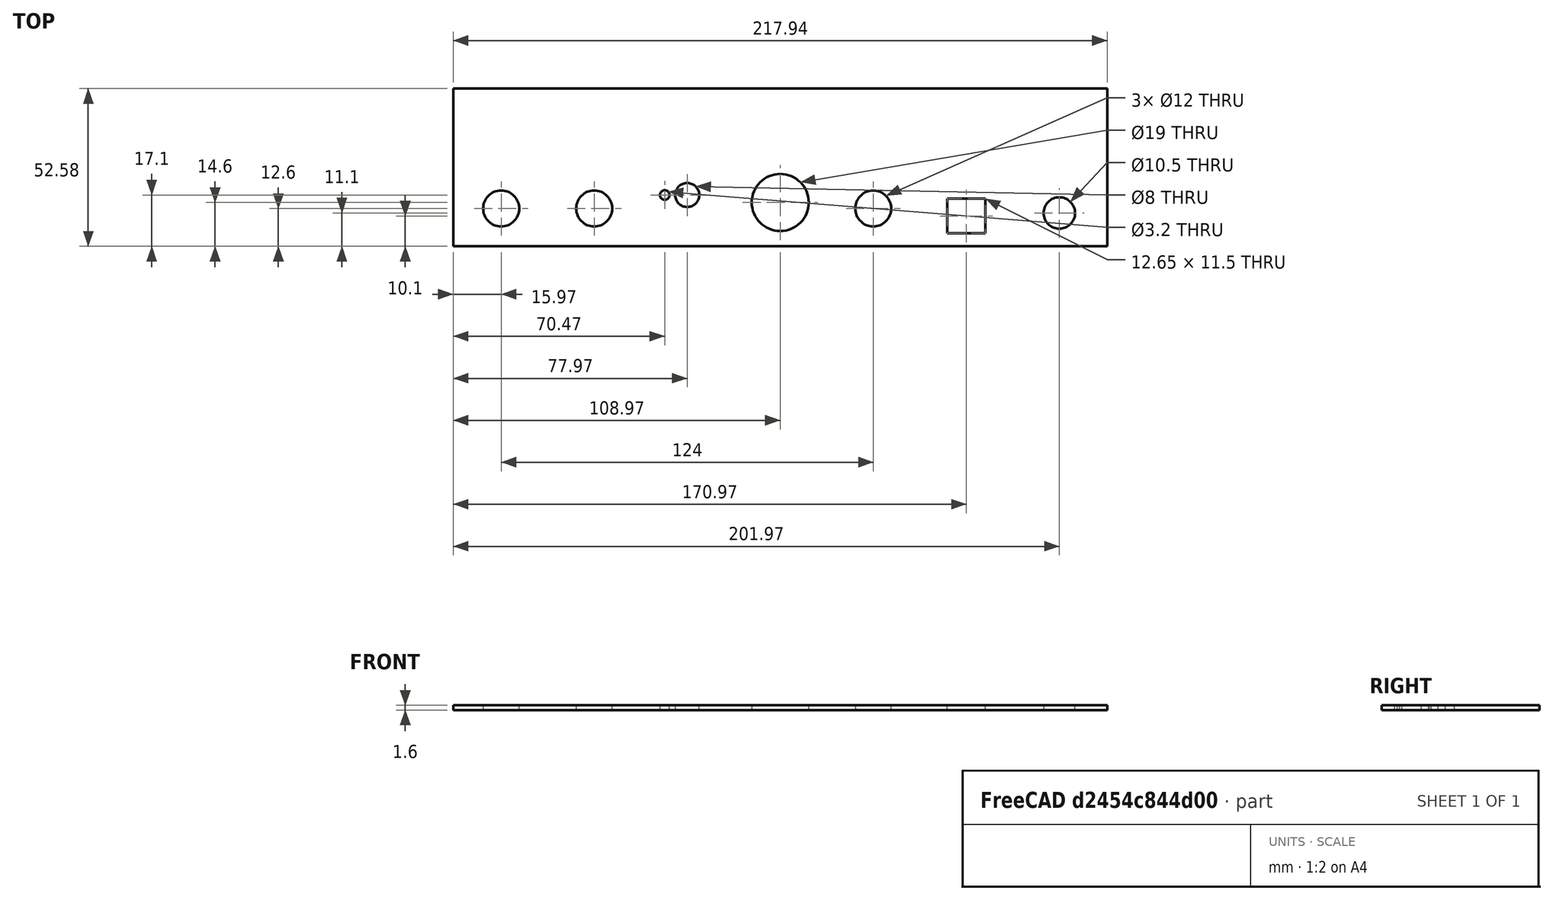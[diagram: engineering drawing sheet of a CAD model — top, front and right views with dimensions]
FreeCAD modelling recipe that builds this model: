
FCSTD DOCUMENT  (FreeCAD 0.21R33771 (Git))
Label: PT-10 Rear
License: All rights reserved
LicenseURL: https://en.wikipedia.org/wiki/All_rights_reserved
objects: Sketcher::SketchObject×1, PartDesign::Pad×1, PartDesign::Body×1
note: 4 computed .brp shape members not serialized (recipe doc carries the construction recipe); baked Part::Feature solids carry a one-line shape summary decoded from their .brp

FEATURE [Sketcher::SketchObject] Sketch
  FullyConstrained = false
  MapMode = 5
  Support = -> [XY_Plane]
  sketch-geometry (19):
    g0: LineSegment StartX=-108.965 StartY=26.29 StartZ=0 EndX=108.965 EndY=26.29 EndZ=0
    g1: LineSegment StartX=108.965 StartY=26.29 StartZ=0 EndX=108.965 EndY=-26.29 EndZ=0
    g2: LineSegment StartX=108.965 StartY=-26.29 StartZ=0 EndX=-108.965 EndY=-26.29 EndZ=0
    g3: LineSegment StartX=-108.965 StartY=-26.29 StartZ=0 EndX=-108.965 EndY=26.29 EndZ=0
    g4: LineSegment StartX=-120.891 StartY=-13.69 StartZ=0 EndX=116.092 EndY=-13.69 EndZ=0
    g5: Circle CenterX=-93 CenterY=-13.69 CenterZ=0 NormalX=0 NormalY=0 NormalZ=1 AngleXU=0 Radius=6
    g6: Circle CenterX=-62 CenterY=-13.69 CenterZ=0 NormalX=0 NormalY=0 NormalZ=1 AngleXU=0 Radius=6
    g7: Circle CenterX=31 CenterY=-13.69 CenterZ=0 NormalX=0 NormalY=0 NormalZ=1 AngleXU=0 Radius=6
    g8: Circle CenterX=-31 CenterY=-9.19 CenterZ=0 NormalX=0 NormalY=0 NormalZ=1 AngleXU=0 Radius=4
    g9: Circle CenterX=-38.5 CenterY=-9.19 CenterZ=0 NormalX=0 NormalY=0 NormalZ=1 AngleXU=0 Radius=1.6
    g10: Circle CenterX=0 CenterY=-11.69 CenterZ=0 NormalX=0 NormalY=0 NormalZ=1 AngleXU=0 Radius=9.5
    g11: LineSegment StartX=62 StartY=-10.44 StartZ=0 EndX=62 EndY=-21.69 EndZ=0
    g12: Circle CenterX=93 CenterY=-15.19 CenterZ=0 NormalX=0 NormalY=0 NormalZ=1 AngleXU=0 Radius=5.25
    g13: LineSegment StartX=-43.3721 StartY=-9.19 StartZ=0 EndX=-17.1069 EndY=-9.19 EndZ=0
    g14: LineSegment StartX=55.675 StartY=-10.44 StartZ=0 EndX=68.325 EndY=-10.44 EndZ=0
    g15: LineSegment StartX=68.325 StartY=-10.44 StartZ=0 EndX=68.325 EndY=-21.94 EndZ=0
    g16: LineSegment StartX=68.325 StartY=-21.94 StartZ=0 EndX=55.675 EndY=-21.94 EndZ=0
    g17: LineSegment StartX=55.675 StartY=-21.94 StartZ=0 EndX=55.675 EndY=-10.44 EndZ=0
    g18: LineSegment StartX=-120.15 StartY=-21.69 StartZ=0 EndX=116.905 EndY=-21.69 EndZ=0
  constraints (53):
    c: Coincident(g0,g1)
    c: Coincident(g1,g2)
    c: Coincident(g2,g3)
    c: Coincident(g3,g0)
    c: Horizontal(g0)
    c: Horizontal(g2)
    c: Vertical(g1)
    c: Vertical(g3)
    c: Symmetric(g1,g0,g-1)
    c: DistanceY(g3,g3) = 52.58
    c: DistanceX(g0,g0) = 217.93
    c: Horizontal(g4)
    c: PointOnObject(g5,g4)
    c: PointOnObject(g6,g4)
    c: PointOnObject(g7,g4)
    c: Equal(g5,g6)
    c: Equal(g6,g7)
    c: DistanceX(g8,g10) = 31
    c: DistanceX(g6,g8) = 31
    c: DistanceX(g5,g6) = 31
    c: DistanceX(g10,g7) = 31
    c: Vertical(g11)
    c: DistanceX(g7,g11) = 31
    c: DistanceX(g11,g12) = 31
    c: Horizontal(g13)
    c: PointOnObject(g8,g13)
    c: PointOnObject(g9,g13)
    c: PointOnObject(g10,g-2)
    c: Coincident(g14,g15)
    c: Coincident(g15,g16)
    c: Coincident(g16,g17)
    c: Coincident(g17,g14)
    c: Horizontal(g14)
    c: Horizontal(g16)
    c: Vertical(g15)
    c: Vertical(g17)
    c: PointOnObject(g11,g14)
    c: Symmetric(g15,g16,g11)
    c: Diameter(g8) = 8
    c: Diameter(g9) = 3.2
    c: Horizontal(g18)
    c: Diameter(g10) = 19
    c: Diameter(g5) = 12
    c: DistanceX(g9,g8) = 7.5
    c: Diameter(g12) = 10.5
    c: DistanceY(g17,g17) = 11.5
    c: DistanceX(g14,g14) = 12.65
    c: DistanceY(g18,g12) = 6.5
    c: DistanceY(g18,g4) = 8
    c: DistanceY(g18,g13) = 12.5
    c: DistanceY(g18,g10) = 10
    c: DistanceY(g1,g18) = 4.6
    c: DistanceY(g16,g18) = 0.25
FEATURE [PartDesign::Pad] Pad
  Direction = (0,0,1)
  Length = 1.6
  Length2 = 10
  Profile = -> Sketch
  ReferenceAxis = -> Sketch [N_Axis]
  Type = 0
FEATURE [PartDesign::Body] Body  label="Corps"
  Group = -> [Sketch,Pad]
  Origin = -> Origin
  Tip = -> Pad
